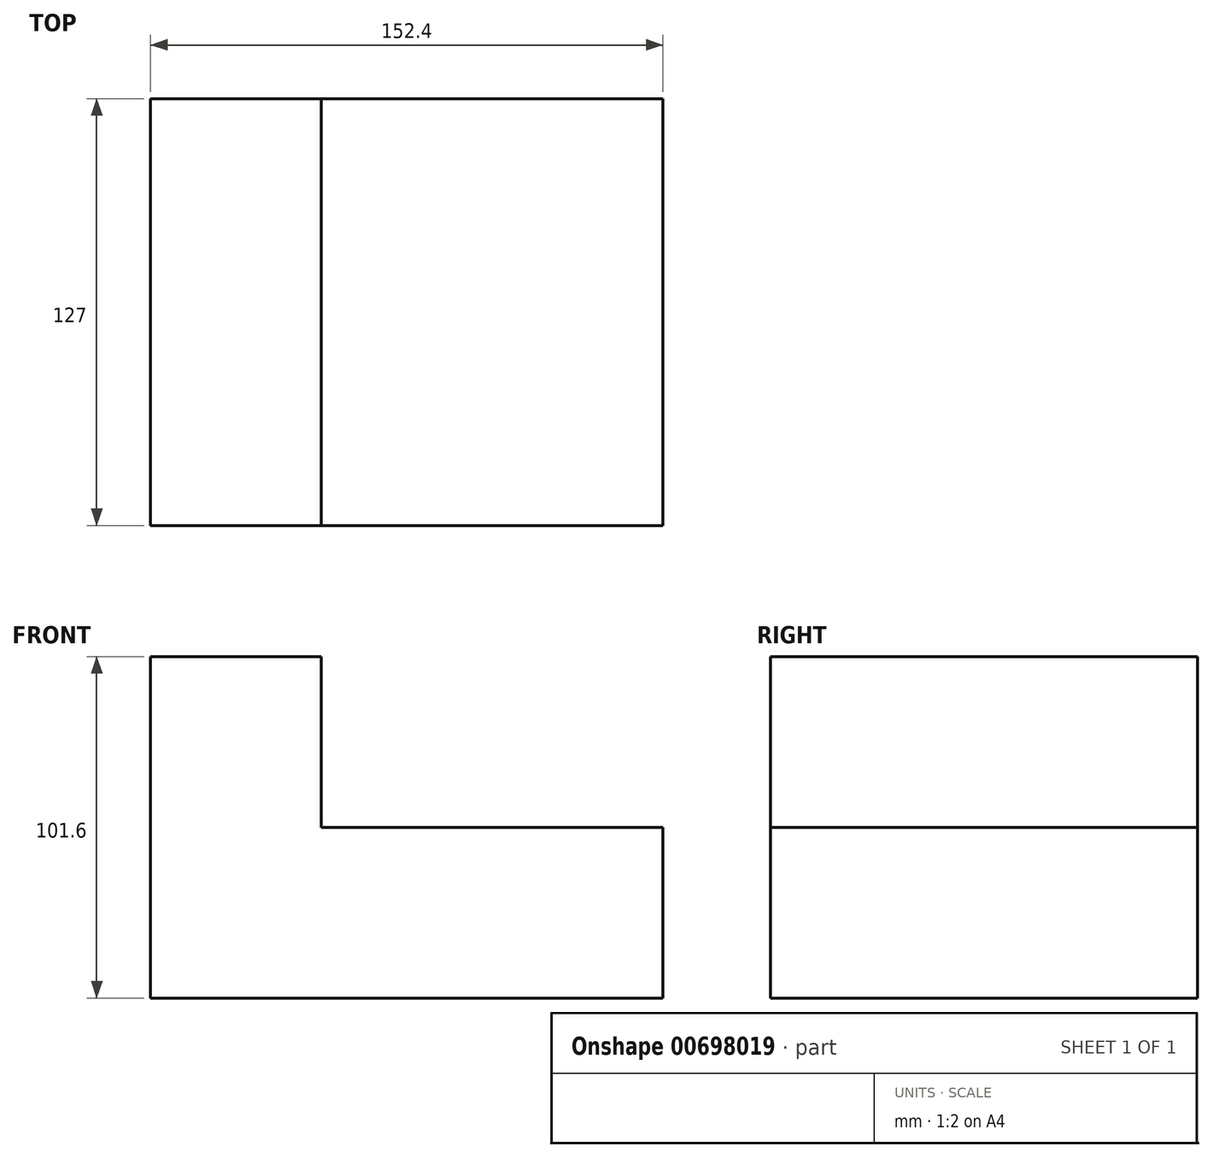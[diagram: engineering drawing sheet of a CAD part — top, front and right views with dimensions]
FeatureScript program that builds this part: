
annotation { "Feature Type Name" : "Feature", "Feature Type Description" : "" }
export const myFeature = defineFeature(function(context is Context, id is Id, definition is map)
    precondition{}
    {
        {
            var Q0;
            Q0=qCreatedBy(makeId("Front.planeOp"),FACE);
            var sketch = newSketch(context, id + "F0", { "sketchPlane" : qUnion([Q0])});
            skLineSegment(sketch, "E0", {"start": v(-125.05, -15.12) * mm, "end": v(27.35, -15.12) * mm});
            skLineSegment(sketch, "E1", {"start": v(27.35, -15.12) * mm, "end": v(27.35, 35.68) * mm});
            skLineSegment(sketch, "E2", {"start": v(27.35, 35.68) * mm, "end": v(-74.25, 35.68) * mm});
            skLineSegment(sketch, "E3", {"start": v(-74.25, 35.68) * mm, "end": v(-74.25, 86.48) * mm});
            skLineSegment(sketch, "E4", {"start": v(-74.25, 86.48) * mm, "end": v(-125.05, 86.48) * mm});
            skLineSegment(sketch, "E5", {"start": v(-125.05, 86.48) * mm, "end": v(-125.05, -15.12) * mm});
            skSolve(sketch);
        }
        {
            var Q0;
            Q0=makeQuery(id+"F0.imprint","IMPRINT",FACE,{"disambiguationData":[TD([[makeQuery(id+"F0.imprint","IMPRINT",EDGE,{"derivedFrom":sQuery(id+"F0.wireOp",EDGE,"E0")}),1.0]])]});
            extrude(context, id + "F1", {"entities" : qUnion([Q0]), "depth" : 127 * mm, "offsetDistance" : 25.4 * mm});
        }
    });
